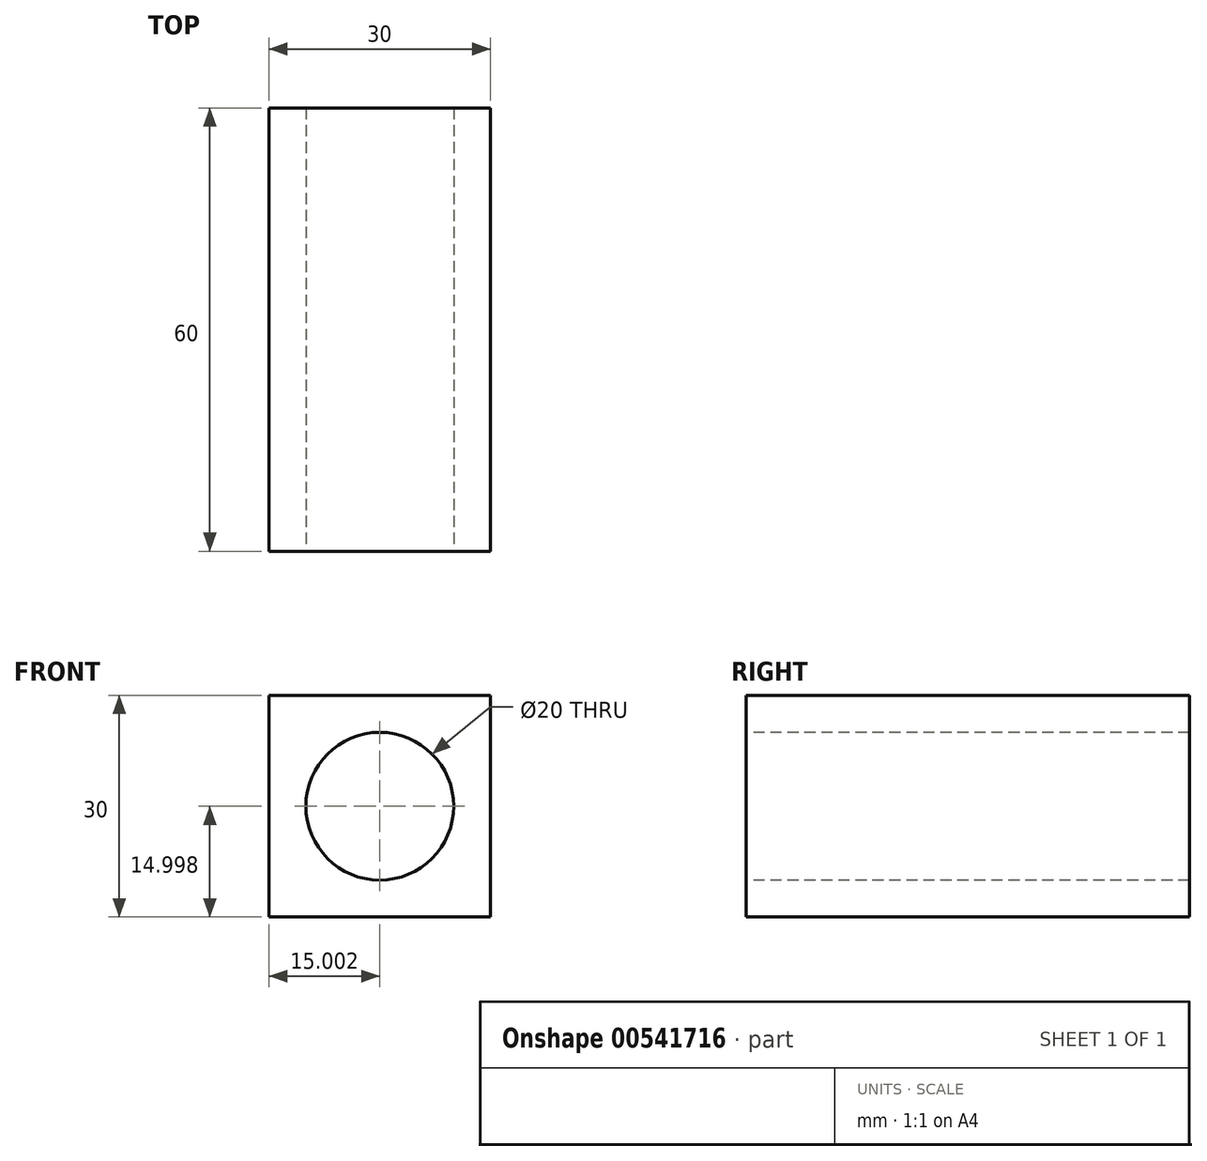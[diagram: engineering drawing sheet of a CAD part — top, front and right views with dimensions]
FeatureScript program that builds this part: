
annotation { "Feature Type Name" : "Feature", "Feature Type Description" : "" }
export const myFeature = defineFeature(function(context is Context, id is Id, definition is map)
    precondition{}
    {
        {
            var Q0;
            Q0=qCreatedBy(makeId("Front.planeOp"),FACE);
            var sketch = newSketch(context, id + "F0", { "sketchPlane" : qUnion([Q0])});
            skLineSegment(sketch, "E0.bottom", {"start": v(-20.32, 16.78) * mm, "end": v(9.68, 16.78) * mm});
            skLineSegment(sketch, "E0.top", {"start": v(-20.32, -13.22) * mm, "end": v(9.68, -13.22) * mm});
            skLineSegment(sketch, "E0.left", {"start": v(-20.32, 16.78) * mm, "end": v(-20.32, -13.22) * mm});
            skLineSegment(sketch, "E0.right", {"start": v(9.68, 16.78) * mm, "end": v(9.68, -13.22) * mm});
            skSolve(sketch);
        }
        {
            var Q0;
            Q0 = qSketchRegion(id + "F0", true);
            extrude(context, id + "F1", {"entities" : qUnion([Q0]), "depth" : 60 * mm, "offsetDistance" : 25 * mm});
        }
        {
            var Q0;
            Q0=makeQuery(id+"F1.opExtrude","CAP_FACE",FACE,{"disambiguationData":[OSD([sQuery(id+"F0.wireOp",EDGE,"E0.bottom"),sQuery(id+"F0.wireOp",EDGE,"E0.top"),sQuery(id+"F0.wireOp",EDGE,"E0.left"),sQuery(id+"F0.wireOp",EDGE,"E0.right")])],"isStart":false});
            var sketch = newSketch(context, id + "F2", { "sketchPlane" : qUnion([Q0])});
            skCircle(sketch, "E1", {"center": v(-5.32, 1.78) * mm, "radius": 10 * mm});
            skPoint(sketch, "E1.centerSnap0", {"position": v(-5.32, 16.78) * mm});
            skPoint(sketch, "E1.centerSnap1", {"position": v(-20.32, 1.78) * mm});
            skSolve(sketch);
        }
        {
            var Q0;
            Q0 = qSketchRegion(id + "F2", true);
            extrude(context, id + "F3", {"entities" : qUnion([Q0]), "operationType" : NewBodyOperationType.REMOVE, "endBound" : BoundingType.UP_TO_NEXT, "oppositeDirection" : true, "depth" : 25 * mm, "offsetDistance" : 25 * mm});
        }
    });
